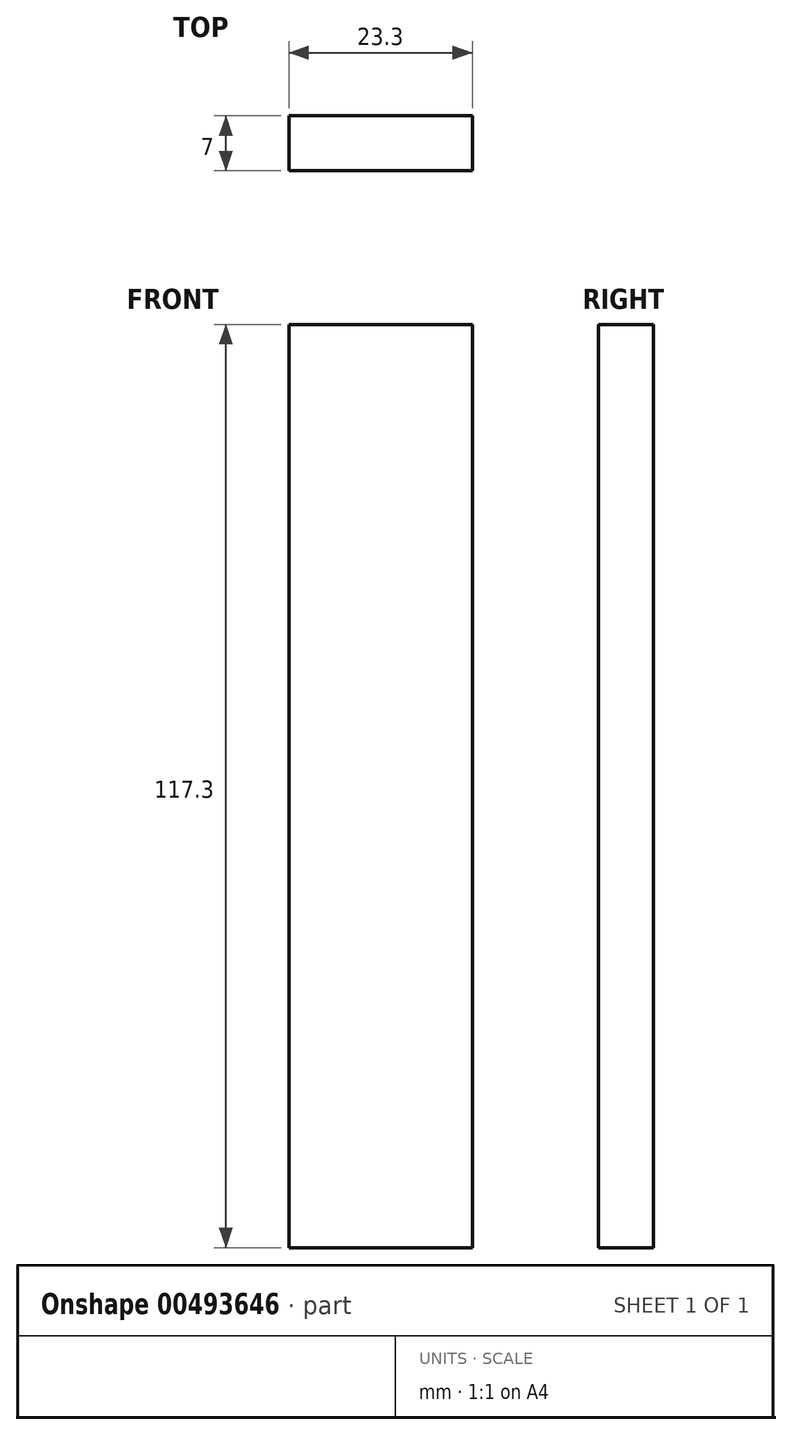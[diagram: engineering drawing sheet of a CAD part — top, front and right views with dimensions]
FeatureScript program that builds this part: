
annotation { "Feature Type Name" : "Feature", "Feature Type Description" : "" }
export const myFeature = defineFeature(function(context is Context, id is Id, definition is map)
    precondition{}
    {
        {
            var Q0;
            Q0=qCreatedBy(makeId("Front.planeOp"),FACE);
            var sketch = newSketch(context, id + "F0", { "sketchPlane" : qUnion([Q0])});
            skLineSegment(sketch, "E0.bottom", {"start": v(-11.65, 58.65) * mm, "end": v(11.65, 58.65) * mm});
            skLineSegment(sketch, "E0.top", {"start": v(-11.65, -58.65) * mm, "end": v(11.65, -58.65) * mm});
            skLineSegment(sketch, "E0.left", {"start": v(-11.65, 58.65) * mm, "end": v(-11.65, -58.65) * mm});
            skLineSegment(sketch, "E0.right", {"start": v(11.65, 58.65) * mm, "end": v(11.65, -58.65) * mm});
            skPoint(sketch, "E0.middle", {"position": v(0, 0) * mm});
            skSolve(sketch);
        }
        {
            var Q0;
            Q0=makeQuery(id+"F0.imprint","IMPRINT",FACE,{"disambiguationData":[TD([[makeQuery(id+"F0.imprint","IMPRINT",EDGE,{"derivedFrom":sQuery(id+"F0.wireOp",EDGE,"E0.bottom")}),-1.0]])]});
            extrude(context, id + "F1", {"entities" : qUnion([Q0]), "endBound" : BoundingType.SYMMETRIC, "depth" : 7 * mm});
        }
    });
